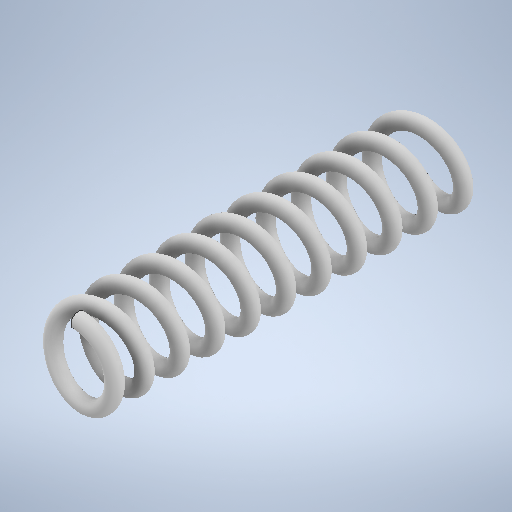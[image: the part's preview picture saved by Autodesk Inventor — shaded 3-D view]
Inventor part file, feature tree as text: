
AUTODESK INVENTOR PART (.ipt)
format: ipt  version: 2025.1 (Build 291241000, 241)  size: 899,072 bytes
history: native  units: mm
features: sketch x4, projected_geometry x3, plane x2, helix x1
ambient origin geometry x8: Origin, YZ Plane, XZ Plane, XY Plane, X Axis, Y Axis, Z Axis, Center Point
bodies: Solid1 (feature_tree)
feature tree (10):
  helix  "Coil1"  [1 undecoded]
  plane  "Work Plane1"
  sketch  "Sketch3"  dims[d3=4.0mm]
  plane  "Work Plane2"
  sketch  "Sketch4"  dims[d4=10.0mm d5=19.8mm d6=100.0mm d7=0.0mm d8=120.0deg d9=90.0deg d10=0.0mm d11=0.0mm]
  sketch  "Sketch5"  dims[d12=0.0mm d13=19.8mm]
  sketch  "Sketch2"  dims[d2=19.8mm]
  projected_geometry  "Projected Loop1"
  projected_geometry  "Projected Loop2"
  projected_geometry  "Projected Loop3"
note: 1 required parameter value undecoded (feature->parameter linkage not recoverable at this tier; creation-order binding heuristic only, values carry confidence <= 0.55)
